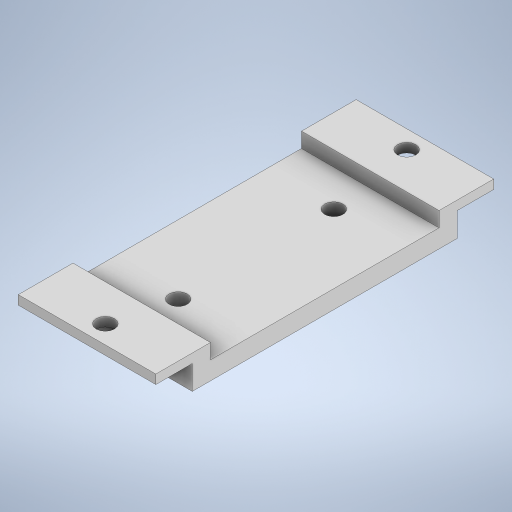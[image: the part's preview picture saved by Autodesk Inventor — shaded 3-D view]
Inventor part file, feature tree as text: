
AUTODESK INVENTOR PART (.ipt)
format: ipt  version: 2023 (Build 270158000, 158)  size: 352,768 bytes
history: native  units: mm
features: extrude x7, sketch x7
ambient origin geometry x8: Origin, YZ Plane, XZ Plane, XY Plane, X Axis, Y Axis, Z Axis, Center Point
bodies: Solid1 (feature_tree)
feature tree (14):
  extrude  "Extrusion1"  Depth=20.0mm
  extrude  "Extrusion2"  Depth=26.0mm
  extrude  "Extrusion3"  Depth=20.0mm
  extrude  "Extrusion4"  Depth=10.0mm
  sketch  "Sketch5"  dims[d9=10.0mm d10=26.0mm]
  extrude  "Extrusion5"  Depth=10.0mm
  extrude  "Extrusion6"  Depth=75.5mm TaperAngle=0.0deg
  extrude  "Extrusion7"  Depth=20.0mm
  sketch  "Sketch1"  dims[d0=20.0mm d1=20.0mm]
  sketch  "Sketch2"  dims[d2=55.5mm d3=26.0mm]
  sketch  "Sketch3"  dims[d5=20.0mm d6=45.5mm]
  sketch  "Sketch4"  dims[d7=20.0mm d8=10.0mm]
  sketch  "Sketch6"  dims[d11=75.5mm d12=0.0mm d13=75.5mm d14=0.0mm]
  sketch  "Sketch7"  dims[d21=65.5mm d22=55.5mm d23=10.0mm d24=10.0mm d25=0.0mm d26=0.0mm d27=18.25mm d28=0.0mm d29=0.0mm d30=5.0mm d31=5.0mm d32=20.0mm d33=0.0mm d34=20.0mm d35=0.0mm d36=10.0mm d37=10.0mm d38=20.0mm d39=0.0mm]
